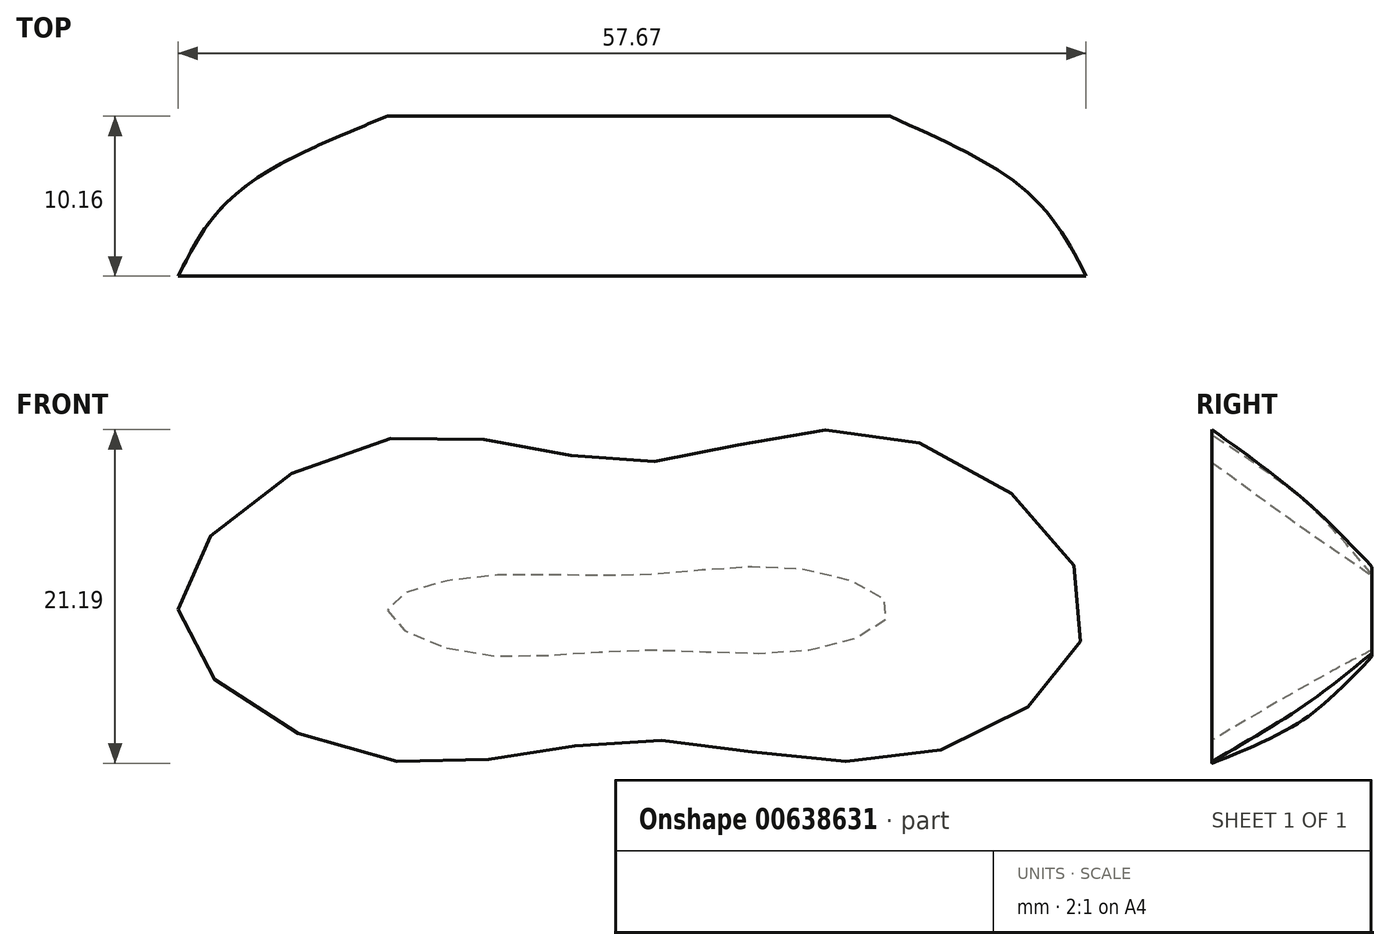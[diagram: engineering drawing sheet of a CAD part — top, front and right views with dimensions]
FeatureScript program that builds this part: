
annotation { "Feature Type Name" : "Feature", "Feature Type Description" : "" }
export const myFeature = defineFeature(function(context is Context, id is Id, definition is map)
    precondition{}
    {
        {
            var Q0;
            Q0=qCreatedBy(makeId("Front.planeOp"),FACE);
            cPlane(context, id + "F0", {"entities" : qUnion([Q0]), "cplaneType" : CPlaneType.OFFSET, "offset" : 6.35 * mm, "oppositeDirection" : true, "width" : 152.4 * mm, "height" : 152.4 * mm});
        }
        {
            var Q0;
            Q0=qCreatedBy(makeId("Front.planeOp"),FACE);
            cPlane(context, id + "F1", {"entities" : qUnion([Q0]), "cplaneType" : CPlaneType.OFFSET, "offset" : 10.16 * mm, "oppositeDirection" : true, "width" : 152.4 * mm, "height" : 152.4 * mm});
        }
        {
            var Q0;
            Q0=qCreatedBy(makeId("Front.planeOp"),FACE);
            var sketch = newSketch(context, id + "F2", { "sketchPlane" : qUnion([Q0])});
            skFitSpline(sketch, "E0", {"points": [v(-29.23, 0) * mm, v(-16.14, 10.8) * mm, v(0, 9.36) * mm, v(15.6, 11.19) * mm, v(28.42, 0) * mm, v(17.57, -9.31) * mm, v(0, -8.28) * mm, v(-16.17, -9.52) * mm, v(-29.23, 0) * mm]});
            skSolve(sketch);
        }
        {
            var Q0;
            Q0=qCreatedBy(id+"F0.planeOp",FACE);
            var sketch = newSketch(context, id + "F3", { "sketchPlane" : qUnion([Q0])});
            skFitSpline(sketch, "E1", {"points": [v(23.4, 0) * mm, v(14, 6.4) * mm, v(0, 4.78) * mm, v(-16.28, 6.24) * mm, v(-24.05, 0) * mm, v(-15.95, -6.4) * mm, v(0, -4.62) * mm, v(14.66, -5.59) * mm, v(23.4, 0) * mm]});
            skSolve(sketch);
        }
        {
            var Q0;
            Q0=qCreatedBy(id+"F1.planeOp",FACE);
            var sketch = newSketch(context, id + "F4", { "sketchPlane" : qUnion([Q0])});
            skFitSpline(sketch, "E2", {"points": [v(15.95, 0) * mm, v(10.56, 2.55) * mm, v(0, 2.19) * mm, v(-10.93, 2.02) * mm, v(-15.95, 0) * mm, v(-11.26, -2.67) * mm, v(0, -2.56) * mm, v(11.3, -2.49) * mm, v(15.95, 0) * mm]});
            skSolve(sketch);
        }
        {
            var Q0;
            Q0=makeQuery(id+"F2.imprint","IMPRINT",FACE,{"disambiguationData":[TD([[makeQuery(id+"F2.imprint","IMPRINT",EDGE,{"derivedFrom":sQuery(id+"F2.wireOp",EDGE,"E0")}),-1.0]])]});
            var Q1;
            Q1=makeQuery(id+"F3.imprint","IMPRINT",FACE,{"disambiguationData":[TD([[makeQuery(id+"F3.imprint","IMPRINT",EDGE,{"derivedFrom":sQuery(id+"F3.wireOp",EDGE,"E1")}),1.0]])]});
            var Q2;
            Q2=makeQuery(id+"F4.imprint","IMPRINT",FACE,{"disambiguationData":[TD([[makeQuery(id+"F4.imprint","IMPRINT",EDGE,{"derivedFrom":sQuery(id+"F4.wireOp",EDGE,"E2")}),1.0]])]});
            loft(context, id + "F5", {"sheetProfilesArray" : [{ "sheetProfileEntities" : qUnion([Q0]) }, { "sheetProfileEntities" : qUnion([Q1]) }, { "sheetProfileEntities" : qUnion([Q2]) }]});
        }
    });
